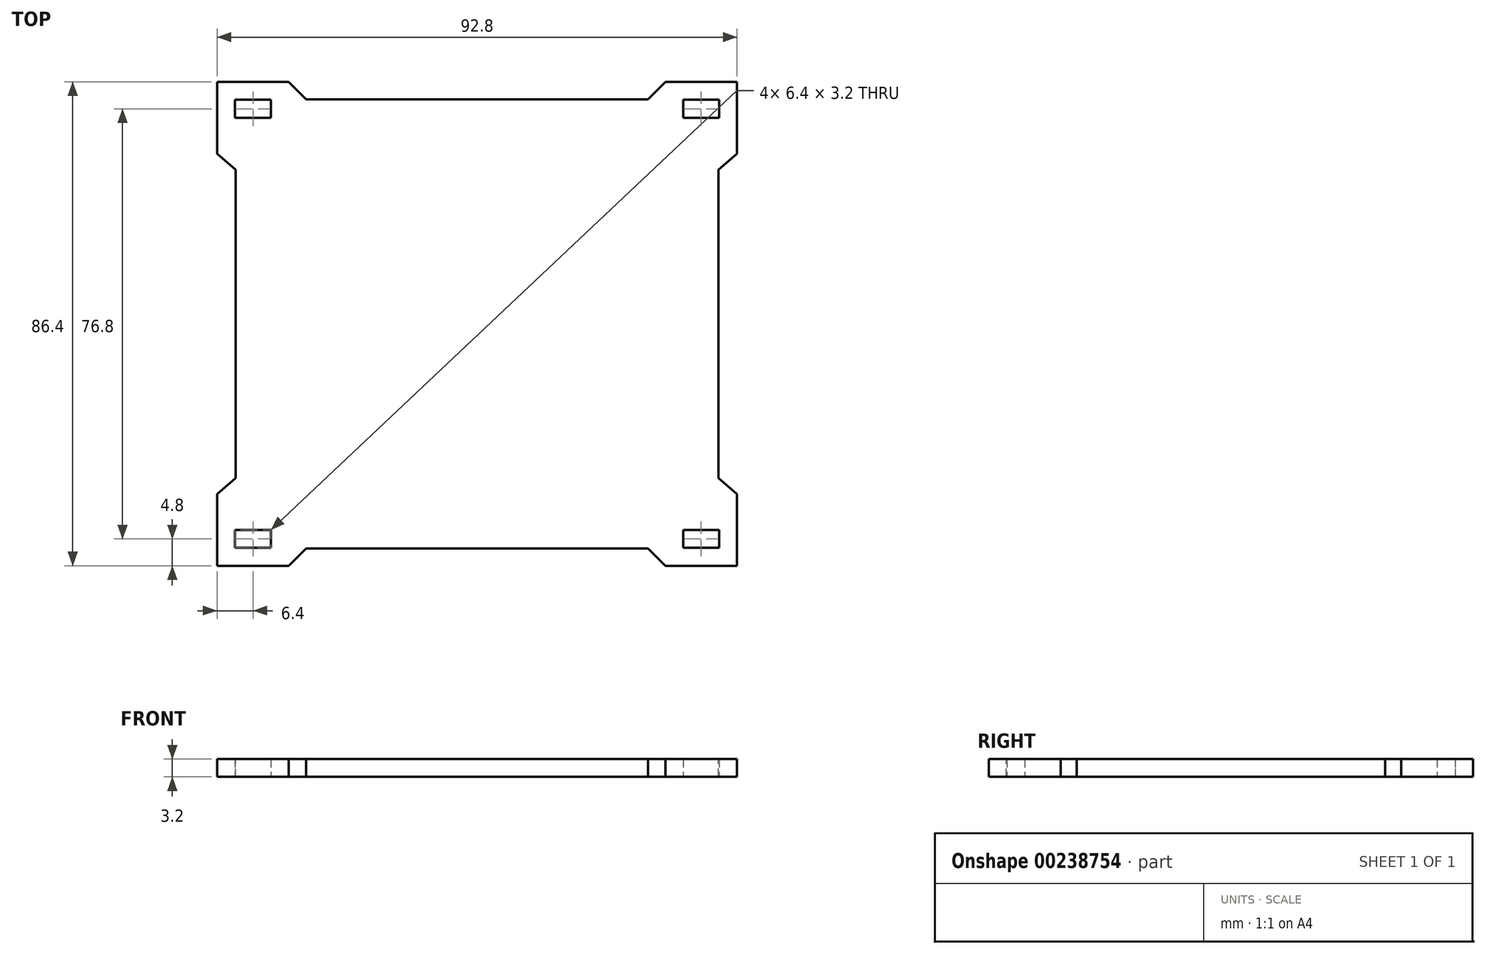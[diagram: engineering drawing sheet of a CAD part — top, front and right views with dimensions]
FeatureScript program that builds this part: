
annotation { "Feature Type Name" : "Feature", "Feature Type Description" : "" }
export const myFeature = defineFeature(function(context is Context, id is Id, definition is map)
    precondition{}
    {
        {
            var Q0;
            Q0=qCreatedBy(makeId("Top.planeOp"),FACE);
            var sketch = newSketch(context, id + "F0", { "sketchPlane" : qUnion([Q0])});
            skLineSegment(sketch, "E0.bottom", {"start": v(46.4, 43.2) * mm, "end": v(-46.4, 43.2) * mm});
            skLineSegment(sketch, "E0.top", {"start": v(46.4, -43.2) * mm, "end": v(-46.4, -43.2) * mm});
            skLineSegment(sketch, "E0.left", {"start": v(46.4, 43.2) * mm, "end": v(46.4, -43.2) * mm});
            skLineSegment(sketch, "E0.right", {"start": v(-46.4, 43.2) * mm, "end": v(-46.4, -43.2) * mm});
            skPoint(sketch, "E0.middle", {"position": v(0, 0) * mm});
            skLineSegment(sketch, "E1.bottom", {"start": v(-43.2, 40) * mm, "end": v(-36.8, 40) * mm});
            skLineSegment(sketch, "E1.top", {"start": v(-43.2, 36.8) * mm, "end": v(-36.8, 36.8) * mm});
            skLineSegment(sketch, "E1.left", {"start": v(-43.2, 40) * mm, "end": v(-43.2, 36.8) * mm});
            skLineSegment(sketch, "E1.right", {"start": v(-36.8, 40) * mm, "end": v(-36.8, 36.8) * mm});
            skLineSegment(sketch, "E2.MirrorCS", {"start": v(43.2, 36.8) * mm, "end": v(36.8, 36.8) * mm});
            skLineSegment(sketch, "E3.MirrorCS", {"start": v(36.8, 40) * mm, "end": v(36.8, 36.8) * mm});
            skLineSegment(sketch, "E4.MirrorCS", {"start": v(43.2, 40) * mm, "end": v(36.8, 40) * mm});
            skLineSegment(sketch, "E5.MirrorCS", {"start": v(43.2, 40) * mm, "end": v(43.2, 36.8) * mm});
            skLineSegment(sketch, "E6.MirrorCS", {"start": v(43.2, -40) * mm, "end": v(43.2, -36.8) * mm});
            skLineSegment(sketch, "E7.MirrorCS", {"start": v(36.8, -40) * mm, "end": v(36.8, -36.8) * mm});
            skLineSegment(sketch, "E8.MirrorCS", {"start": v(-36.8, -40) * mm, "end": v(-36.8, -36.8) * mm});
            skLineSegment(sketch, "E9.MirrorCS", {"start": v(-43.2, -40) * mm, "end": v(-43.2, -36.8) * mm});
            skLineSegment(sketch, "E10.MirrorCS", {"start": v(43.2, -40) * mm, "end": v(36.8, -40) * mm});
            skLineSegment(sketch, "E11.MirrorCS", {"start": v(-43.2, -36.8) * mm, "end": v(-36.8, -36.8) * mm});
            skLineSegment(sketch, "E12.MirrorCS", {"start": v(43.2, -36.8) * mm, "end": v(36.8, -36.8) * mm});
            skLineSegment(sketch, "E13.MirrorCS", {"start": v(-43.2, -40) * mm, "end": v(-36.8, -40) * mm});
            skSolve(sketch);
        }
        {
            var Q0;
            Q0 = qSketchRegion(id + "F0", true);
            extrude(context, id + "F1", {"entities" : qUnion([Q0]), "depth" : 3.2 * mm});
        }
        {
            var Q0;
            Q0=makeQuery(id+"F1.opExtrude","CAP_FACE",FACE,{"disambiguationData":[OSD([sQuery(id+"F0.wireOp",EDGE,"E0.bottom"),sQuery(id+"F0.wireOp",EDGE,"E0.top"),sQuery(id+"F0.wireOp",EDGE,"E0.left"),sQuery(id+"F0.wireOp",EDGE,"E0.right"),sQuery(id+"F0.wireOp",EDGE,"E1.bottom"),sQuery(id+"F0.wireOp",EDGE,"E1.top"),sQuery(id+"F0.wireOp",EDGE,"E1.left"),sQuery(id+"F0.wireOp",EDGE,"E1.right"),sQuery(id+"F0.wireOp",EDGE,"E2.MirrorCS"),sQuery(id+"F0.wireOp",EDGE,"E3.MirrorCS"),sQuery(id+"F0.wireOp",EDGE,"E4.MirrorCS"),sQuery(id+"F0.wireOp",EDGE,"E5.MirrorCS"),sQuery(id+"F0.wireOp",EDGE,"E6.MirrorCS"),sQuery(id+"F0.wireOp",EDGE,"E7.MirrorCS"),sQuery(id+"F0.wireOp",EDGE,"E8.MirrorCS"),sQuery(id+"F0.wireOp",EDGE,"E9.MirrorCS"),sQuery(id+"F0.wireOp",EDGE,"E10.MirrorCS"),sQuery(id+"F0.wireOp",EDGE,"E11.MirrorCS"),sQuery(id+"F0.wireOp",EDGE,"E12.MirrorCS"),sQuery(id+"F0.wireOp",EDGE,"E13.MirrorCS")])],"isStart":false});
            var sketch = newSketch(context, id + "F2", { "sketchPlane" : qUnion([Q0])});
            skLineSegment(sketch, "E14", {"start": v(33.6, -43.2) * mm, "end": v(30.5, -40.1) * mm});
            skLineSegment(sketch, "E15", {"start": v(30.5, -40.1) * mm, "end": v(0, -40.1) * mm});
            skLineSegment(sketch, "E16.MirrorCS", {"start": v(-30.5, -40.1) * mm, "end": v(0, -40.1) * mm});
            skLineSegment(sketch, "E17.MirrorCS", {"start": v(-33.6, -43.2) * mm, "end": v(-30.5, -40.1) * mm});
            skLineSegment(sketch, "E18", {"start": v(33.6, -43.2) * mm, "end": v(-33.6, -43.2) * mm});
            skLineSegment(sketch, "E19.MirrorCS", {"start": v(-33.6, 43.2) * mm, "end": v(-30.5, 40.1) * mm});
            skLineSegment(sketch, "E20.MirrorCS", {"start": v(33.6, 43.2) * mm, "end": v(-33.6, 43.2) * mm});
            skLineSegment(sketch, "E21.MirrorCS", {"start": v(-30.5, 40.1) * mm, "end": v(0, 40.1) * mm});
            skLineSegment(sketch, "E22.MirrorCS", {"start": v(30.5, 40.1) * mm, "end": v(0, 40.1) * mm});
            skLineSegment(sketch, "E23.MirrorCS", {"start": v(33.6, 43.2) * mm, "end": v(30.5, 40.1) * mm});
            skLineSegment(sketch, "E24.MirrorCS", {"start": v(46.4, -30.4) * mm, "end": v(43.09, -27.53) * mm});
            skLineSegment(sketch, "E25", {"start": v(43.09, -27.53) * mm, "end": v(43.09, 0) * mm});
            skLineSegment(sketch, "E26.MirrorCS", {"start": v(43.09, 27.53) * mm, "end": v(43.09, 0) * mm});
            skLineSegment(sketch, "E27.MirrorCS", {"start": v(46.4, 30.4) * mm, "end": v(43.09, 27.53) * mm});
            skLineSegment(sketch, "E28", {"start": v(46.4, 30.4) * mm, "end": v(46.4, -30.4) * mm});
            skLineSegment(sketch, "E29.MirrorCS", {"start": v(-46.4, 30.4) * mm, "end": v(-46.4, -30.4) * mm});
            skLineSegment(sketch, "E30.MirrorCS", {"start": v(-46.4, 30.4) * mm, "end": v(-43.09, 27.53) * mm});
            skLineSegment(sketch, "E31.MirrorCS", {"start": v(-46.4, -30.4) * mm, "end": v(-43.09, -27.53) * mm});
            skLineSegment(sketch, "E32.MirrorCS", {"start": v(-43.09, -27.53) * mm, "end": v(-43.09, 0) * mm});
            skLineSegment(sketch, "E33.MirrorCS", {"start": v(-43.09, 27.53) * mm, "end": v(-43.09, 0) * mm});
            skSolve(sketch);
        }
        {
            var Q0;
            Q0 = qSketchRegion(id + "F2", true);
            extrude(context, id + "F3", {"entities" : qUnion([Q0]), "operationType" : NewBodyOperationType.REMOVE, "endBound" : BoundingType.THROUGH_ALL, "oppositeDirection" : true, "depth" : 25 * mm});
        }
    });
